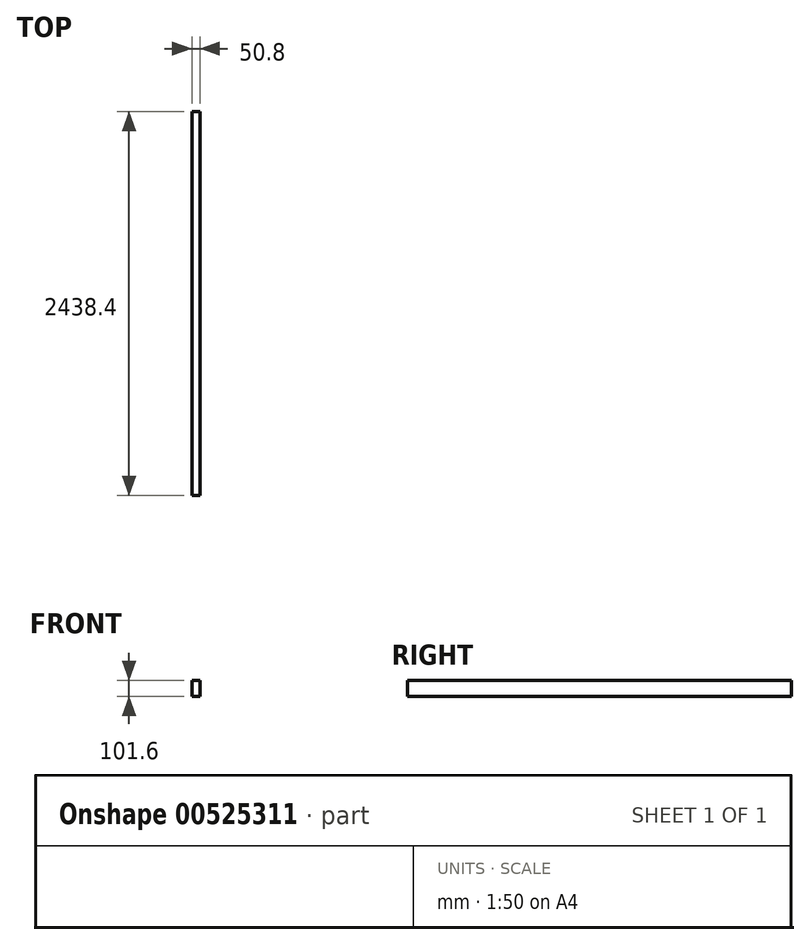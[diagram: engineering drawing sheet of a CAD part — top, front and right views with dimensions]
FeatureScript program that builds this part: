
annotation { "Feature Type Name" : "Feature", "Feature Type Description" : "" }
export const myFeature = defineFeature(function(context is Context, id is Id, definition is map)
    precondition{}
    {
        {
            var Q0;
            Q0=qCreatedBy(makeId("Front.planeOp"),FACE);
            var sketch = newSketch(context, id + "F0", { "sketchPlane" : qUnion([Q0])});
            skLineSegment(sketch, "E0.bottom", {"start": v(0, 0) * mm, "end": v(50.8, 0) * mm});
            skLineSegment(sketch, "E0.top", {"start": v(0, 101.6) * mm, "end": v(50.8, 101.6) * mm});
            skLineSegment(sketch, "E0.left", {"start": v(0, 0) * mm, "end": v(0, 101.6) * mm});
            skLineSegment(sketch, "E0.right", {"start": v(50.8, 0) * mm, "end": v(50.8, 101.6) * mm});
            skSolve(sketch);
        }
        {
            var Q0;
            Q0=makeQuery(id+"F0.imprint","IMPRINT",FACE,{"disambiguationData":[TD([[makeQuery(id+"F0.imprint","IMPRINT",EDGE,{"derivedFrom":sQuery(id+"F0.wireOp",EDGE,"E0.bottom")}),1.0]])]});
            extrude(context, id + "F1", {"entities" : qUnion([Q0]), "depth" : 2438.4 * mm, "offsetDistance" : 25.4 * mm});
        }
    });
